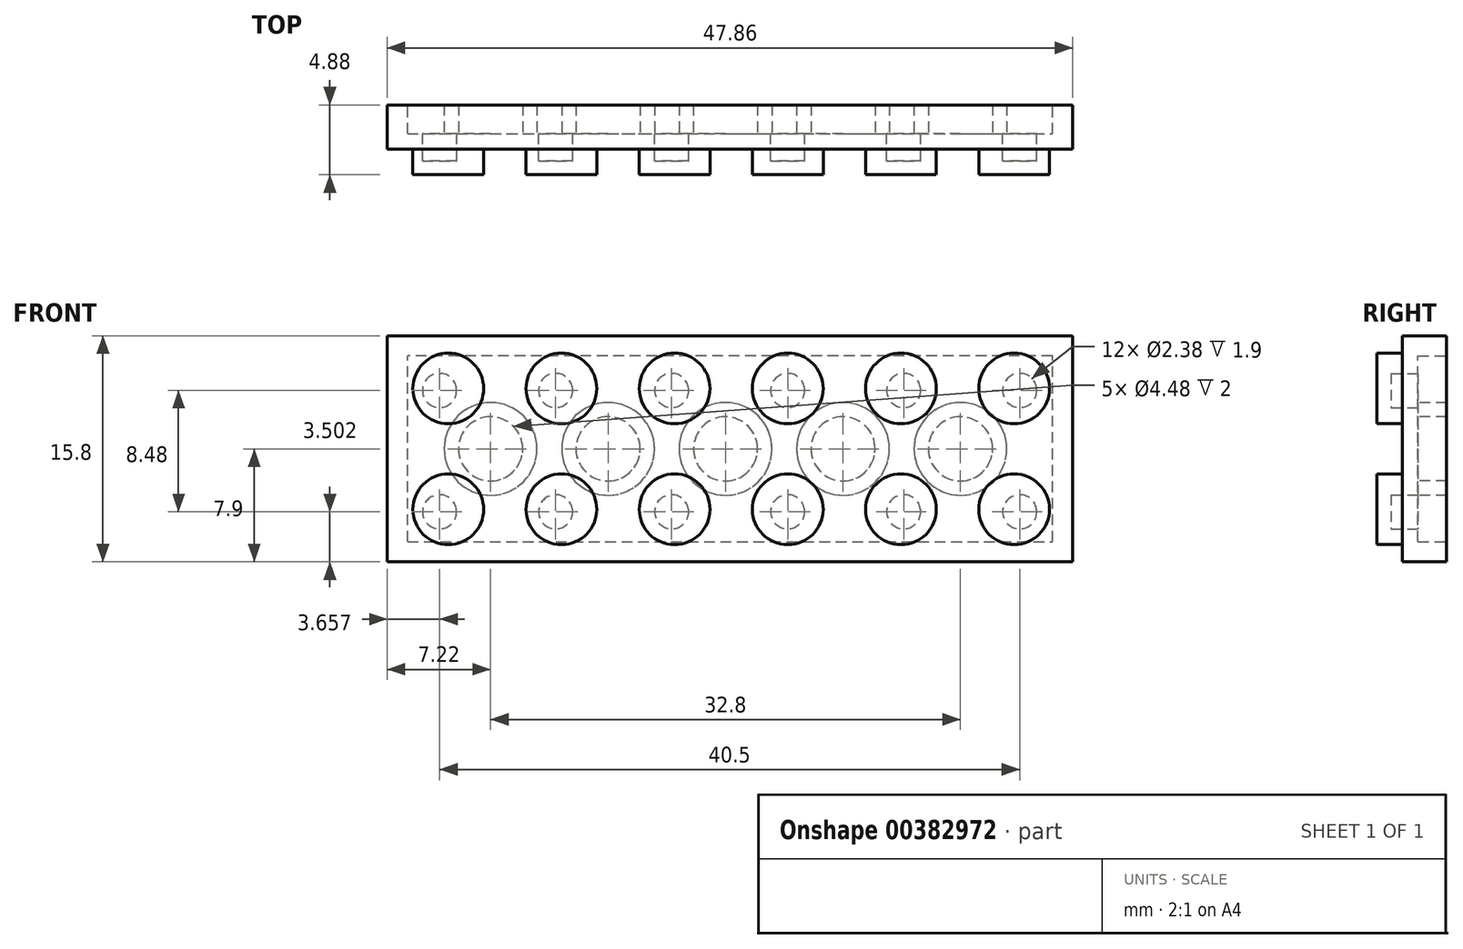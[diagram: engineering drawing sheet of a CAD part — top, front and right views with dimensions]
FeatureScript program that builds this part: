
annotation { "Feature Type Name" : "Feature", "Feature Type Description" : "" }
export const myFeature = defineFeature(function(context is Context, id is Id, definition is map)
    precondition{}
    {
        {
            var Q0;
            Q0=qCreatedBy(makeId("Front.planeOp"),FACE);
            var sketch = newSketch(context, id + "F0", { "sketchPlane" : qUnion([Q0])});
            skLineSegment(sketch, "E0", {"start": v(0, 0) * mm, "end": v(0, 15.8) * mm});
            skLineSegment(sketch, "E1", {"start": v(0, 15.8) * mm, "end": v(47.86, 15.8) * mm});
            skLineSegment(sketch, "E2", {"start": v(47.86, 15.8) * mm, "end": v(47.86, 0) * mm});
            skLineSegment(sketch, "E3", {"start": v(47.86, 0) * mm, "end": v(0, 0) * mm});
            skSolve(sketch);
        }
        {
            var Q0;
            Q0=qSketchRegion(id+"F0",true);
            extrude(context, id + "F1", {"entities" : qUnion([Q0]), "depth" : 3.09 * mm});
        }
        {
            var Q0;
            Q0=makeQuery(id+"F1.opExtrude","CAP_FACE",FACE,{"disambiguationData":[OSD([sQuery(id+"F0.wireOp",EDGE,"E0"),sQuery(id+"F0.wireOp",EDGE,"E1"),sQuery(id+"F0.wireOp",EDGE,"E2"),sQuery(id+"F0.wireOp",EDGE,"E3")])],"isStart":false});
            var sketch = newSketch(context, id + "F2", { "sketchPlane" : qUnion([Q0])});
            skCircle(sketch, "E4", {"center": v(4.26, 12.12) * mm, "radius": 2.47 * mm});
            skCircle(sketch, "E5.1.0.0", {"center": v(12.16, 12.12) * mm, "radius": 2.47 * mm});
            skCircle(sketch, "E5.2.0.0", {"center": v(20.06, 12.12) * mm, "radius": 2.47 * mm});
            skCircle(sketch, "E5.3.0.0", {"center": v(27.96, 12.12) * mm, "radius": 2.47 * mm});
            skCircle(sketch, "E5.4.0.0", {"center": v(35.86, 12.12) * mm, "radius": 2.47 * mm});
            skCircle(sketch, "E5.5.0.0", {"center": v(43.76, 12.12) * mm, "radius": 2.47 * mm});
            skCircle(sketch, "E6", {"center": v(4.26, 3.67) * mm, "radius": 2.47 * mm});
            skCircle(sketch, "E7.1.0.0", {"center": v(12.16, 3.67) * mm, "radius": 2.47 * mm});
            skCircle(sketch, "E7.2.0.0", {"center": v(20.06, 3.67) * mm, "radius": 2.47 * mm});
            skCircle(sketch, "E7.3.0.0", {"center": v(27.96, 3.67) * mm, "radius": 2.47 * mm});
            skCircle(sketch, "E7.4.0.0", {"center": v(35.86, 3.67) * mm, "radius": 2.47 * mm});
            skCircle(sketch, "E7.5.0.0", {"center": v(43.76, 3.67) * mm, "radius": 2.47 * mm});
            skLineSegment(sketch, "E7.direction1", {"start": v(4.26, 3.67) * mm, "end": v(12.16, 3.67) * mm, "construction": true});
            skSolve(sketch);
        }
        {
            var Q0;
            Q0=qSketchRegion(id+"F2",true);
            extrude(context, id + "F3", {"entities" : qUnion([Q0]), "operationType" : NewBodyOperationType.ADD, "depth" : 1.79 * mm});
        }
        {
            var Q0;
            Q0=makeQuery(id+"F1.opExtrude","CAP_FACE",FACE,{"disambiguationData":[OSD([sQuery(id+"F0.wireOp",EDGE,"E0"),sQuery(id+"F0.wireOp",EDGE,"E1"),sQuery(id+"F0.wireOp",EDGE,"E2"),sQuery(id+"F0.wireOp",EDGE,"E3")])],"isStart":true});
            var sketch = newSketch(context, id + "F4", { "sketchPlane" : qUnion([Q0])});
            skLineSegment(sketch, "E8.right", {"start": v(-1.42, 1.42) * mm, "end": v(-1.42, 14.38) * mm});
            skLineSegment(sketch, "E9", {"start": v(-1.42, 1.42) * mm, "end": v(-46.44, 1.42) * mm});
            skLineSegment(sketch, "E10", {"start": v(-46.44, 1.42) * mm, "end": v(-46.44, 14.38) * mm});
            skLineSegment(sketch, "E11", {"start": v(-46.44, 14.38) * mm, "end": v(-1.42, 14.38) * mm});
            skSolve(sketch);
        }
        {
            var Q0;
            Q0=qSketchRegion(id+"F4",true);
            extrude(context, id + "F5", {"entities" : qUnion([Q0]), "operationType" : NewBodyOperationType.REMOVE, "oppositeDirection" : true, "depth" : 2 * mm});
        }
        {
            var Q0;
            Q0=makeQuery(id+"F5.boolean.opBoolean","COPY",FACE,{"derivedFrom":makeQuery(id+"F5.opExtrude","CAP_FACE",FACE,{"disambiguationData":[OSD([sQuery(id+"F4.wireOp",EDGE,"E8.right"),sQuery(id+"F4.wireOp",EDGE,"E9"),sQuery(id+"F4.wireOp",EDGE,"E10"),sQuery(id+"F4.wireOp",EDGE,"E11")])],"isStart":false})});
            var sketch = newSketch(context, id + "F6", { "sketchPlane" : qUnion([Q0])});
            skCircle(sketch, "E12", {"center": v(-40.02, 7.9) * mm, "radius": 3.24 * mm});
            skPoint(sketch, "E12.centerSnap0", {"position": v(-46.44, 7.9) * mm});
            skCircle(sketch, "E13.1.0.0", {"center": v(-31.82, 7.9) * mm, "radius": 3.24 * mm});
            skCircle(sketch, "E13.2.0.0", {"center": v(-23.62, 7.9) * mm, "radius": 3.24 * mm});
            skCircle(sketch, "E13.3.0.0", {"center": v(-15.42, 7.9) * mm, "radius": 3.24 * mm});
            skCircle(sketch, "E13.4.0.0", {"center": v(-7.22, 7.9) * mm, "radius": 3.24 * mm});
            skLineSegment(sketch, "E13.direction1", {"start": v(-40.02, 7.9) * mm, "end": v(-31.82, 7.9) * mm, "construction": true});
            skSolve(sketch);
        }
        {
            var Q0;
            Q0=qSketchRegion(id+"F6",true);
            var Q1;
            Q1=makeQuery(id+"F1.opExtrude","CAP_FACE",FACE,{"disambiguationData":[OSD([sQuery(id+"F0.wireOp",EDGE,"E0"),sQuery(id+"F0.wireOp",EDGE,"E1"),sQuery(id+"F0.wireOp",EDGE,"E2"),sQuery(id+"F0.wireOp",EDGE,"E3")])],"isStart":true});
            extrude(context, id + "F7", {"entities" : qUnion([Q0]), "operationType" : NewBodyOperationType.ADD, "endBound" : BoundingType.UP_TO_SURFACE, "endBoundEntityFace" : qUnion([Q1]), "depth" : 25 * mm});
        }
        {
            var Q0;
            Q0=makeQuery(id+"F5.boolean.opBoolean","COPY",FACE,{"derivedFrom":makeQuery(id+"F5.opExtrude","CAP_FACE",FACE,{"disambiguationData":[OSD([sQuery(id+"F4.wireOp",EDGE,"E8.right"),sQuery(id+"F4.wireOp",EDGE,"E9"),sQuery(id+"F4.wireOp",EDGE,"E10"),sQuery(id+"F4.wireOp",EDGE,"E11")])],"isStart":false})});
            var sketch = newSketch(context, id + "F8", { "sketchPlane" : qUnion([Q0])});
            skCircle(sketch, "E14", {"center": v(-40.02, 7.9) * mm, "radius": 2.24 * mm});
            skCircle(sketch, "E15.1.0.0", {"center": v(-31.82, 7.9) * mm, "radius": 2.24 * mm});
            skCircle(sketch, "E15.2.0.0", {"center": v(-23.62, 7.9) * mm, "radius": 2.24 * mm});
            skCircle(sketch, "E15.3.0.0", {"center": v(-15.42, 7.9) * mm, "radius": 2.24 * mm});
            skCircle(sketch, "E15.4.0.0", {"center": v(-7.22, 7.9) * mm, "radius": 2.24 * mm});
            skLineSegment(sketch, "E15.direction1", {"start": v(-40.02, 7.9) * mm, "end": v(-31.82, 7.9) * mm, "construction": true});
            skSolve(sketch);
        }
        {
            var Q0;
            Q0=qSketchRegion(id+"F8",true);
            extrude(context, id + "F9", {"entities" : qUnion([Q0]), "operationType" : NewBodyOperationType.REMOVE, "depth" : 2.2 * mm});
        }
        {
            var Q0;
            Q0=makeQuery(id+"F5.boolean.opBoolean","COPY",FACE,{"derivedFrom":makeQuery(id+"F5.opExtrude","CAP_FACE",FACE,{"disambiguationData":[OSD([sQuery(id+"F4.wireOp",EDGE,"E8.right"),sQuery(id+"F4.wireOp",EDGE,"E9"),sQuery(id+"F4.wireOp",EDGE,"E10"),sQuery(id+"F4.wireOp",EDGE,"E11")])],"isStart":false})});
            var sketch = newSketch(context, id + "F10", { "sketchPlane" : qUnion([Q0])});
            skCircle(sketch, "E16", {"center": v(-44.16, 11.98) * mm, "radius": 1.19 * mm});
            skCircle(sketch, "E17", {"center": v(-44.16, 3.5) * mm, "radius": 1.19 * mm});
            skCircle(sketch, "E18.1.0.0", {"center": v(-36.06, 11.98) * mm, "radius": 1.19 * mm});
            skCircle(sketch, "E18.1.0.1", {"center": v(-36.06, 3.5) * mm, "radius": 1.19 * mm});
            skCircle(sketch, "E18.2.0.0", {"center": v(-27.96, 11.98) * mm, "radius": 1.19 * mm});
            skCircle(sketch, "E18.2.0.1", {"center": v(-27.96, 3.5) * mm, "radius": 1.19 * mm});
            skCircle(sketch, "E18.3.0.0", {"center": v(-19.86, 11.98) * mm, "radius": 1.19 * mm});
            skCircle(sketch, "E18.3.0.1", {"center": v(-19.86, 3.5) * mm, "radius": 1.19 * mm});
            skCircle(sketch, "E18.4.0.0", {"center": v(-11.76, 11.98) * mm, "radius": 1.19 * mm});
            skCircle(sketch, "E18.4.0.1", {"center": v(-11.76, 3.5) * mm, "radius": 1.19 * mm});
            skCircle(sketch, "E18.5.0.0", {"center": v(-3.66, 11.98) * mm, "radius": 1.19 * mm});
            skCircle(sketch, "E18.5.0.1", {"center": v(-3.66, 3.5) * mm, "radius": 1.19 * mm});
            skLineSegment(sketch, "E18.direction1", {"start": v(-44.16, 11.98) * mm, "end": v(-36.06, 11.98) * mm, "construction": true});
            skSolve(sketch);
        }
        {
            var Q0;
            Q0=qSketchRegion(id+"F10",true);
            extrude(context, id + "F11", {"entities" : qUnion([Q0]), "operationType" : NewBodyOperationType.REMOVE, "oppositeDirection" : true, "depth" : 1.9 * mm});
        }
    });
